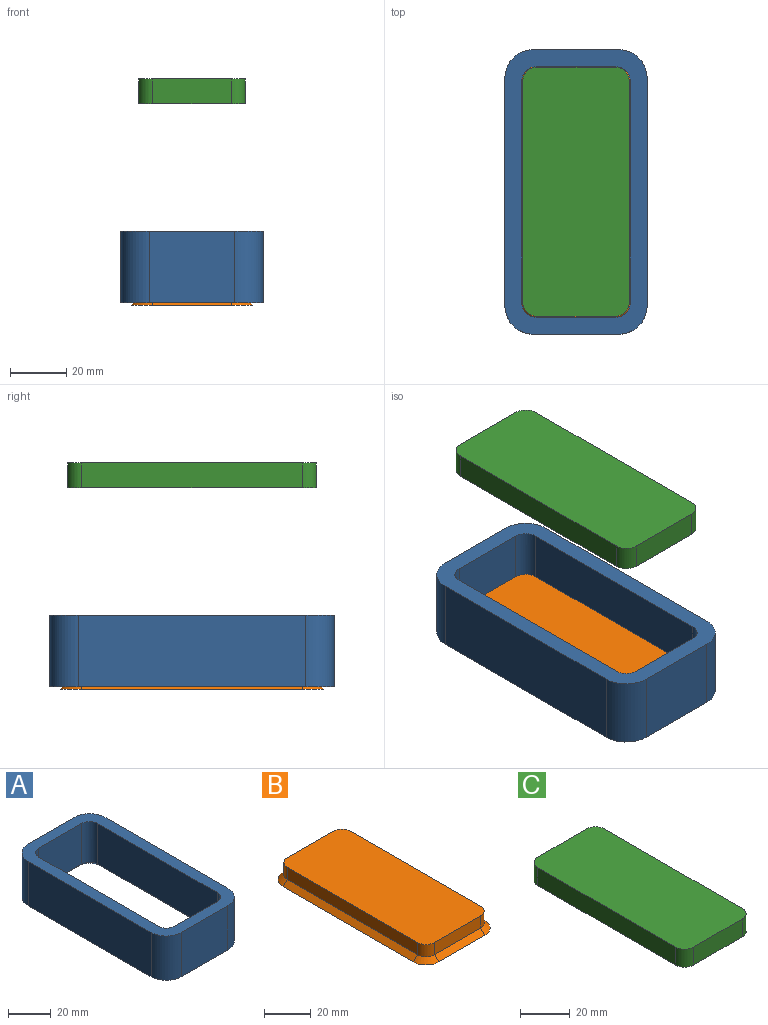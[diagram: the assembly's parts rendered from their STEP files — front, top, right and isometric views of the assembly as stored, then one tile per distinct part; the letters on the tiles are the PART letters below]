
ASSEMBLY  parts=3 mates=2
PART A: 26 faces, bbox 50.8x101.6x25.4 mm
  f0: plane 81.28x25.4mm, normal (1,0,0), area 2064.5mm2, adj f4,f9,f14,f17
  f1: plane 30.48x25.4mm, normal (0,1,0), area 774.2mm2, adj f4,f9,f14,f15
  f2: plane 81.28x25.4mm, normal (-1,0,0), area 2064.5mm2, adj f4,f9,f15,f16
  f3: plane 30.48x25.4mm, normal (0,-1,0), area 774.2mm2, adj f4,f9,f16,f17
  f4: plane 101.6x50.8mm, normal (0,0,-1), area 1064.5mm2, adj f0,f1,f2,f3,f14,f15,f16,f17
  f5: plane 79.36x23.18mm, normal (1,0,0), area 1838.1mm2, adj f9,f10,f13,f19,f21,f23
  f6: plane 28.56x23.18mm, normal (0,-1,0), area 661.3mm2, adj f9,f10,f11,f23,f24,f25
  f7: plane 79.36x23.18mm, normal (-1,0,0), area 1838.1mm2, adj f9,f11,f12,f20,f22,f24
  f8: plane 28.56x23.18mm, normal (0,1,0), area 661.3mm2, adj f9,f12,f13,f18,f19,f20
  f9: plane 101.6x50.8mm, normal (0,0,1), area 1629.9mm2, adj f0,f1,f2,f3,f5,f6,f7,f8
  f10: cylinder r=5.08mm len=23.29mm, axis (0,0,-1), area 185.5mm2, adj f5,f6,f9,f23
  f11: cylinder r=5.08mm len=23.29mm, axis (0,0,1), area 185.5mm2, adj f6,f7,f9,f24
  f12: cylinder r=5.08mm len=23.29mm, axis (0,0,-1), area 185.5mm2, adj f7,f8,f9,f20
  f13: cylinder r=5.08mm len=23.29mm, axis (0,0,1), area 185.5mm2, adj f5,f8,f9,f19
  f14: cylinder r=10.16mm len=25.4mm, axis (0,0,1), area 405.4mm2, adj f0,f1,f4,f9
  f15: cylinder r=10.16mm len=25.4mm, axis (0,0,-1), area 405.4mm2, adj f1,f2,f4,f9
  f16: cylinder r=10.16mm len=25.4mm, axis (0,0,1), area 405.4mm2, adj f2,f3,f4,f9
  f17: cylinder r=10.16mm len=25.4mm, axis (0,0,-1), area 405.4mm2, adj f0,f3,f4,f9
  f18: plane 27.94x2.24mm, normal (0,0.71,-0.71), area 88.3mm2, adj f4,f8,f19,f20
  f19: cone r=7.62mm half-angle=45deg, axis (0,0,-1), area 31.3mm2, adj f4,f5,f8,f13,f18,f21
  f20: cone r=7.62mm half-angle=45deg, axis (0,0,-1), area 31.3mm2, adj f4,f7,f8,f12,f18,f22
  f21: plane 78.74x2.24mm, normal (0.71,0,-0.71), area 248.9mm2, adj f4,f5,f19,f23
  f22: plane 78.74x2.24mm, normal (-0.71,0,-0.71), area 248.9mm2, adj f4,f7,f20,f24
  f23: cone r=7.62mm half-angle=45deg, axis (0,0,-1), area 31.3mm2, adj f4,f5,f6,f10,f21,f25
  f24: cone r=7.62mm half-angle=45deg, axis (0,0,-1), area 31.3mm2, adj f4,f6,f7,f11,f22,f25
  f25: plane 27.94x2.24mm, normal (0,-0.71,-0.71), area 88.3mm2, adj f4,f6,f23,f24
PART B: 18 faces, bbox 43.2x94x8.9 mm
  f0: plane 93.98x43.18mm, normal (0,0,-1), area 4008.2mm2, adj f9,f10,f11,f12,f13,f14,f15,f16
  f1: plane 78.74x6.35mm, normal (-1,0,0), area 500mm2, adj f5,f8,f12,f17
  f2: plane 27.94x6.35mm, normal (0,1,0), area 177.4mm2, adj f5,f6,f16,f17
  f3: plane 78.74x6.35mm, normal (1,0,0), area 500mm2, adj f6,f7,f13,f17
  f4: plane 27.94x6.35mm, normal (0,-1,0), area 177.4mm2, adj f7,f8,f9,f17
  f5: cylinder r=5.08mm len=6.35mm, axis (0,0,-1), area 50.7mm2, adj f1,f2,f14,f17
  f6: cylinder r=5.08mm len=6.35mm, axis (0,0,1), area 50.7mm2, adj f2,f3,f15,f17
  f7: cylinder r=5.08mm len=6.35mm, axis (0,0,-1), area 50.7mm2, adj f3,f4,f11,f17
  f8: cylinder r=5.08mm len=6.35mm, axis (0,0,1), area 50.7mm2, adj f1,f4,f10,f17
  f9: plane 27.94x2.54mm, normal (0,-0.71,0.71), area 100.4mm2, adj f0,f4,f10,f11
  f10: cone r=7.62mm half-angle=45deg, axis (0,0,-1), area 35.8mm2, adj f0,f8,f9,f12
  f11: cone r=7.62mm half-angle=45deg, axis (0,0,-1), area 35.8mm2, adj f0,f7,f9,f13
  f12: plane 78.74x2.54mm, normal (-0.71,0,0.71), area 282.8mm2, adj f0,f1,f10,f14
  f13: plane 78.74x2.54mm, normal (0.71,0,0.71), area 282.8mm2, adj f0,f3,f11,f15
  f14: cone r=7.62mm half-angle=45deg, axis (0,0,-1), area 35.8mm2, adj f0,f5,f12,f16
  f15: cone r=7.62mm half-angle=45deg, axis (0,0,-1), area 35.8mm2, adj f0,f6,f13,f16
  f16: plane 27.94x2.54mm, normal (0,0.71,0.71), area 100.4mm2, adj f0,f2,f14,f15
  f17: plane 88.9x38.1mm, normal (0,0,1), area 3364.9mm2, adj f1,f2,f3,f4,f5,f6,f7,f8
PART C: 10 faces, bbox 38.1x88.9x8.9 mm
  f0: plane 27.94x8.89mm, normal (0,1,0), area 248.4mm2, adj f1,f7,f8,f9
  f1: cylinder r=5.08mm len=8.89mm, axis (0,0,-1), area 70.9mm2, adj f0,f2,f8,f9
  f2: plane 78.74x8.89mm, normal (-1,0,0), area 700mm2, adj f1,f3,f8,f9
  f3: cylinder r=5.08mm len=8.89mm, axis (0,0,-1), area 70.9mm2, adj f2,f4,f8,f9
  f4: plane 27.94x8.89mm, normal (0,-1,0), area 248.4mm2, adj f3,f5,f8,f9
  f5: cylinder r=5.08mm len=8.89mm, axis (0,0,-1), area 70.9mm2, adj f4,f6,f8,f9
  f6: plane 78.74x8.89mm, normal (1,0,0), area 700mm2, adj f5,f7,f8,f9
  f7: cylinder r=5.08mm len=8.89mm, axis (0,0,-1), area 70.9mm2, adj f0,f6,f8,f9
  f8: plane 88.9x38.1mm, normal (0,0,1), area 3364.9mm2, adj f0,f1,f2,f3,f4,f5,f6,f7
  f9: plane 88.9x38.1mm, normal (0,0,-1), area 3364.9mm2, adj f0,f1,f2,f3,f4,f5,f6,f7
PLACE A t=(3.04,-10.04,-24.63)mm fixed
PLACE B t=(3.04,-10.04,-25.54)mm
PLACE C t=(3.04,-10.04,37.42)mm
MATE slider B.f6 <-> A.f24  axis (0,0,1) through (17.01,29.33,-16.65)mm
MATE slider C.f7 <-> A.f24  axis (0,0,1) through (17.01,29.33,55.2)mm
